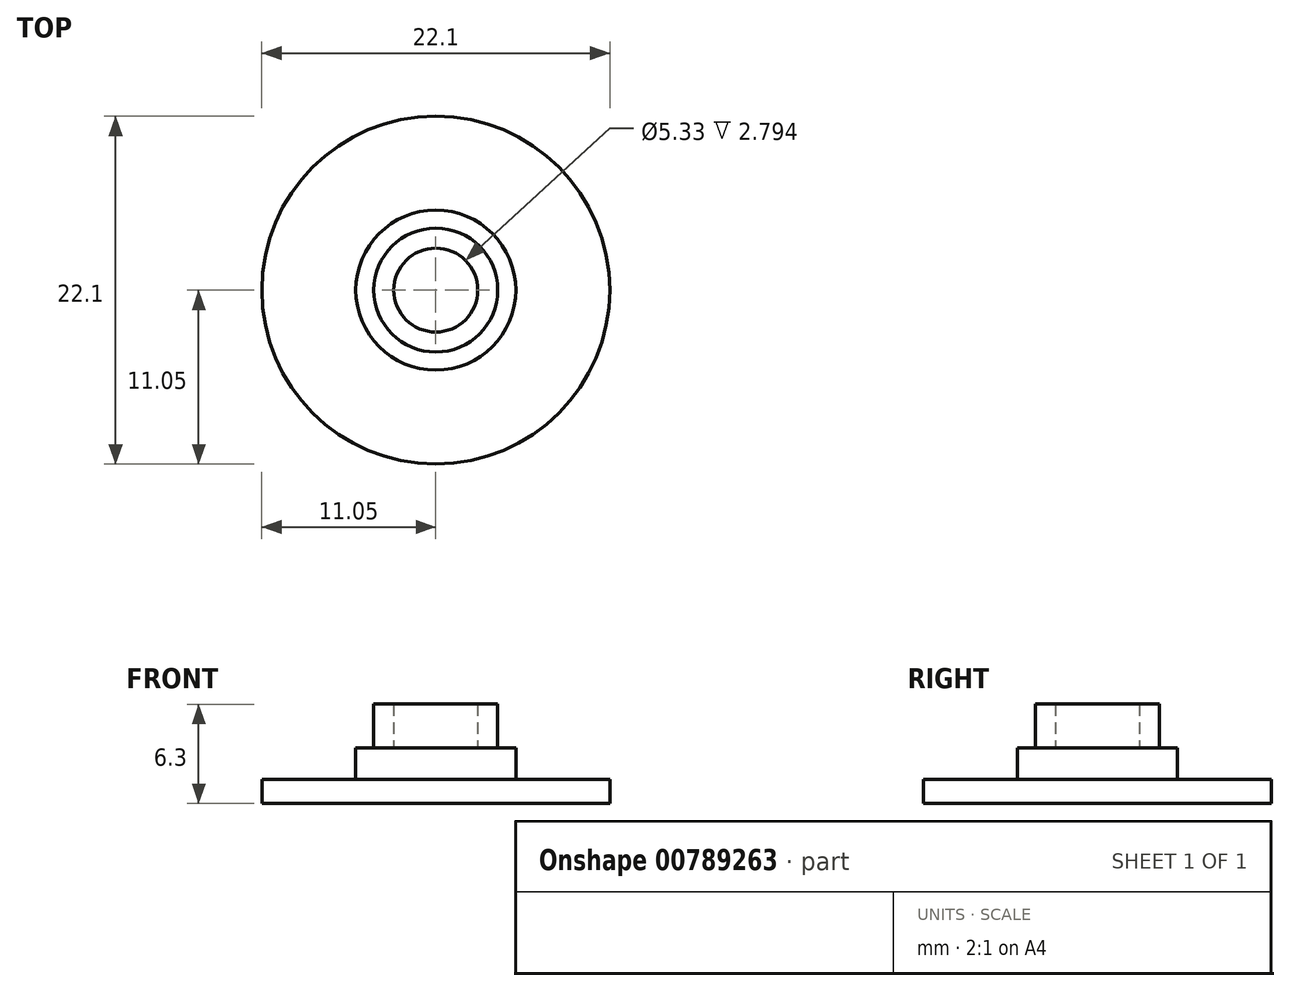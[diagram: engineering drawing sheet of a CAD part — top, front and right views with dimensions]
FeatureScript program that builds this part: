
annotation { "Feature Type Name" : "Feature", "Feature Type Description" : "" }
export const myFeature = defineFeature(function(context is Context, id is Id, definition is map)
    precondition{}
    {
        {
            var Q0;
            Q0=qCreatedBy(makeId("Top.planeOp"),FACE);
            var sketch = newSketch(context, id + "F0", { "sketchPlane" : qUnion([Q0])});
            skCircle(sketch, "E0", {"center": v(0, 0) * mm, "radius": 3.94 * mm});
            skCircle(sketch, "E1.0", {"center": v(0, 0) * mm, "radius": 2.67 * mm});
            skSolve(sketch);
        }
        {
            var Q0;
            Q0=qSketchRegion(id+"F0",true);
            extrude(context, id + "F1", {"entities" : qUnion([Q0]), "depth" : 2.8 * mm, "offsetDistance" : 25.4 * mm});
        }
        {
            var Q0;
            Q0=makeQuery(id+"F1.opExtrude","CAP_FACE",FACE,{"disambiguationData":[OSD([sQuery(id+"F0.wireOp",EDGE,"E0"),sQuery(id+"F0.wireOp",EDGE,"E1.0")])],"isStart":true});
            var sketch = newSketch(context, id + "F2", { "sketchPlane" : qUnion([Q0])});
            skCircle(sketch, "E2", {"center": v(0, 0) * mm, "radius": 5.08 * mm});
            skSolve(sketch);
        }
        {
            var Q0;
            Q0=qSketchRegion(id+"F2",true);
            extrude(context, id + "F3", {"entities" : qUnion([Q0]), "operationType" : NewBodyOperationType.ADD, "depth" : 1.98 * mm, "offsetDistance" : 25.4 * mm});
        }
        {
            var Q0;
            Q0=makeQuery(id+"F3.opExtrude","CAP_FACE",FACE,{"disambiguationData":[OSD([sQuery(id+"F2.wireOp",EDGE,"E2")])],"isStart":false});
            var sketch = newSketch(context, id + "F4", { "sketchPlane" : qUnion([Q0])});
            skCircle(sketch, "E3", {"center": v(0, 0) * mm, "radius": 11.05 * mm});
            skSolve(sketch);
        }
        {
            var Q0;
            Q0=qSketchRegion(id+"F4",true);
            extrude(context, id + "F5", {"entities" : qUnion([Q0]), "operationType" : NewBodyOperationType.ADD, "depth" : 1.52 * mm, "offsetDistance" : 25.4 * mm});
        }
    });
